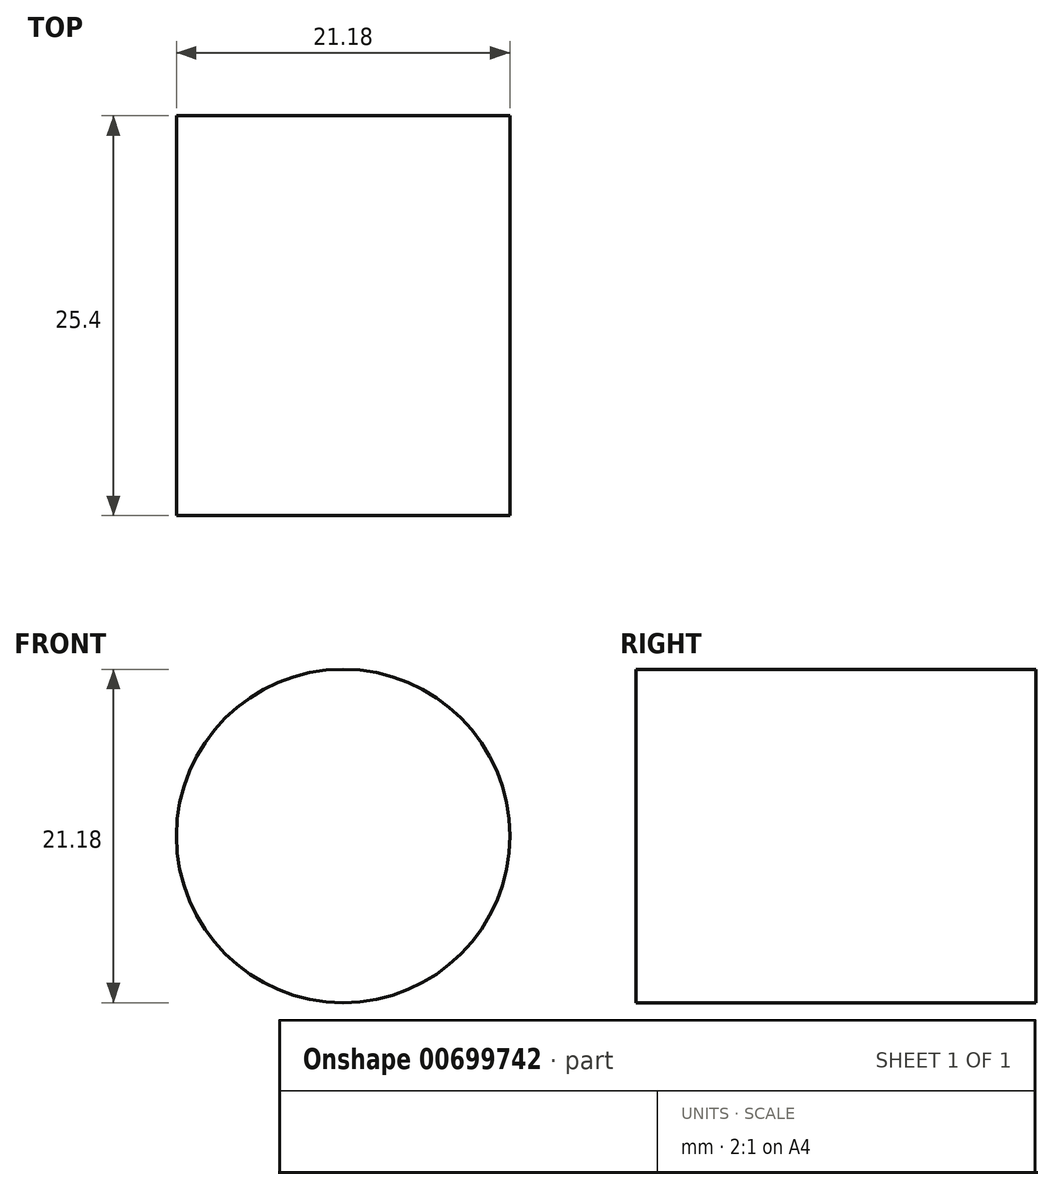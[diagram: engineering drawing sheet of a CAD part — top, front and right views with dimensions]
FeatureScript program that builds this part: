
annotation { "Feature Type Name" : "Feature", "Feature Type Description" : "" }
export const myFeature = defineFeature(function(context is Context, id is Id, definition is map)
    precondition{}
    {
        {
            var Q0;
            Q0=qCreatedBy(makeId("Front.planeOp"),FACE);
            var sketch = newSketch(context, id + "F0", { "sketchPlane" : qUnion([Q0])});
            skCircle(sketch, "E0", {"center": v(0, 0) * mm, "radius": 10.59 * mm});
            skSolve(sketch);
        }
        {
            var Q0;
            Q0=makeQuery(id+"F0.imprint","IMPRINT",FACE,{"disambiguationData":[TD([[makeQuery(id+"F0.imprint","IMPRINT",EDGE,{"derivedFrom":sQuery(id+"F0.wireOp",EDGE,"E0")}),1.0]])]});
            extrude(context, id + "F1", {"entities" : qUnion([Q0]), "depth" : 25.4 * mm, "offsetDistance" : 25.4 * mm});
        }
    });
